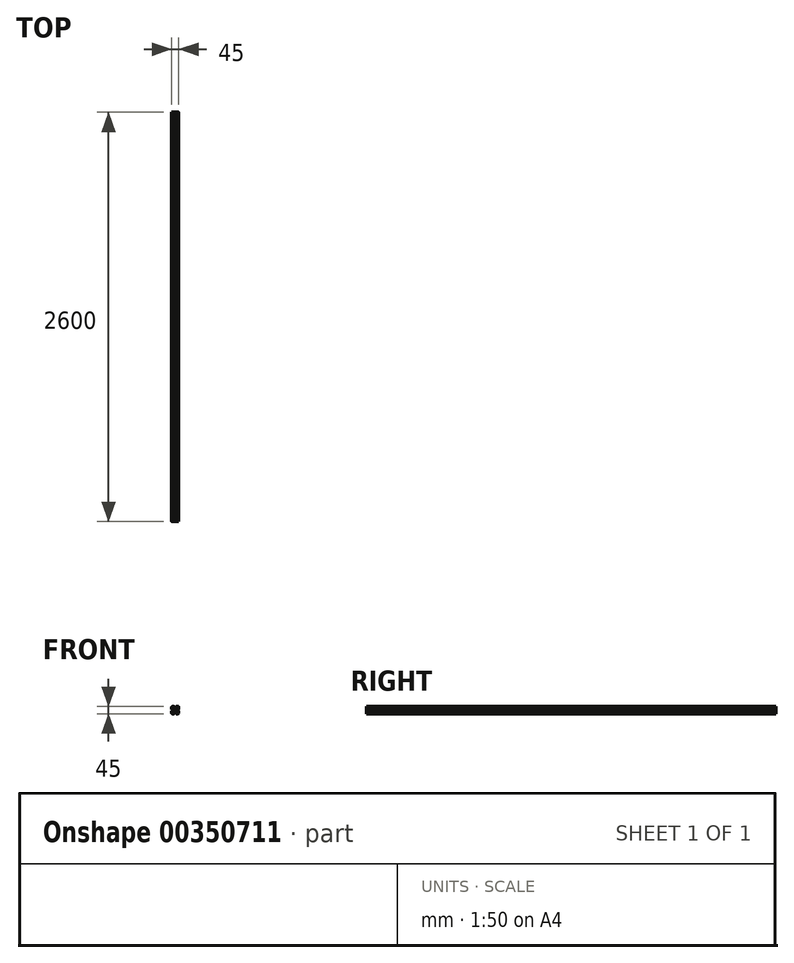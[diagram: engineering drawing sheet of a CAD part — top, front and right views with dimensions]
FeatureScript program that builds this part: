
annotation { "Feature Type Name" : "Feature", "Feature Type Description" : "" }
export const myFeature = defineFeature(function(context is Context, id is Id, definition is map)
    precondition{}
    {
        {
            var Q0;
            Q0=qCreatedBy(makeId("Front.planeOp"),FACE);
            var sketch = newSketch(context, id + "F0", { "sketchPlane" : qUnion([Q0])});
            skLineSegment(sketch, "E0", {"start": v(80.5, 122.5) * mm, "end": v(93.5, 122.5) * mm});
            skLineSegment(sketch, "E1", {"start": v(95, 121) * mm, "end": v(95, 116.5) * mm});
            skLineSegment(sketch, "E2", {"start": v(95, 116.5) * mm, "end": v(90, 116.5) * mm});
            skLineSegment(sketch, "E3", {"start": v(90, 116.5) * mm, "end": v(90, 112.5) * mm});
            skLineSegment(sketch, "E4", {"start": v(90, 112.5) * mm, "end": v(95, 107.5) * mm});
            skLineSegment(sketch, "E5", {"start": v(95, 107.5) * mm, "end": v(100, 107.5) * mm});
            skLineSegment(sketch, "E6", {"start": v(95, 121) * mm, "end": v(94.5, 121) * mm});
            skLineSegment(sketch, "E7", {"start": v(94.5, 121) * mm, "end": v(94.5, 121.5) * mm});
            skPoint(sketch, "E8.orphan", {"position": v(95, 122.5) * mm});
            skPoint(sketch, "E9.visualSharp", {"position": v(94.5, 122.5) * mm});
            skArc(sketch, "E9.filletArc", {"start": v(94.5, 121.5) * mm, "mid": v(94.2, 122.2) * mm, "end": v(93.5, 122.5) * mm});
            skPoint(sketch, "E10.visualSharp", {"position": v(77.5, 122.5) * mm});
            skArc(sketch, "E10.filletArc", {"start": v(80.5, 122.5) * mm, "mid": v(79.35, 122.27) * mm, "end": v(78.38, 121.62) * mm});
            skLineSegment(sketch, "E11.4", {"start": v(-7, 19.5) * mm, "end": v(-7, 19.5) * mm});
            skLineSegment(sketch, "E11.11", {"start": v(-19.5, 7) * mm, "end": v(-19.5, 7) * mm});
            skLineSegment(sketch, "E12", {"start": v(77.5, 122.5) * mm, "end": v(100, 100) * mm, "construction": true});
            skLineSegment(sketch, "E13.MirrorCS", {"start": v(92.5, 105) * mm, "end": v(92.5, 100) * mm});
            skLineSegment(sketch, "E14.MirrorCS", {"start": v(87.5, 110) * mm, "end": v(92.5, 105) * mm});
            skLineSegment(sketch, "E15.MirrorCS", {"start": v(83.5, 110) * mm, "end": v(87.5, 110) * mm});
            skLineSegment(sketch, "E16.MirrorCS", {"start": v(83.5, 105) * mm, "end": v(83.5, 110) * mm});
            skLineSegment(sketch, "E17.MirrorCS", {"start": v(79, 105) * mm, "end": v(83.5, 105) * mm});
            skLineSegment(sketch, "E18.MirrorCS", {"start": v(79, 105) * mm, "end": v(79, 105.5) * mm});
            skLineSegment(sketch, "E19.MirrorCS", {"start": v(79, 105.5) * mm, "end": v(78.5, 105.5) * mm});
            skArc(sketch, "E20.MirrorCS", {"start": v(78.5, 105.5) * mm, "mid": v(77.8, 105.8) * mm, "end": v(77.5, 106.5) * mm});
            skLineSegment(sketch, "E21.MirrorCS", {"start": v(77.5, 119.5) * mm, "end": v(77.5, 106.5) * mm});
            skArc(sketch, "E22.MirrorCS", {"start": v(77.5, 119.5) * mm, "mid": v(77.73, 120.65) * mm, "end": v(78.38, 121.62) * mm});
            skLineSegment(sketch, "E23.MirrorCS", {"start": v(105, 121) * mm, "end": v(105.5, 121) * mm});
            skLineSegment(sketch, "E24.MirrorCS", {"start": v(105.5, 121) * mm, "end": v(105.5, 121.5) * mm});
            skLineSegment(sketch, "E25.MirrorCS", {"start": v(121, 105.5) * mm, "end": v(121.5, 105.5) * mm});
            skLineSegment(sketch, "E26.MirrorCS", {"start": v(121, 105) * mm, "end": v(121, 105.5) * mm});
            skArc(sketch, "E27.MirrorCS", {"start": v(105.5, 121.5) * mm, "mid": v(105.8, 122.2) * mm, "end": v(106.5, 122.5) * mm});
            skLineSegment(sketch, "E28.MirrorCS", {"start": v(110, 116.5) * mm, "end": v(110, 112.5) * mm});
            skArc(sketch, "E29.MirrorCS", {"start": v(122.5, 119.5) * mm, "mid": v(122.27, 120.65) * mm, "end": v(121.62, 121.62) * mm});
            skLineSegment(sketch, "E30.MirrorCS", {"start": v(112.5, 110) * mm, "end": v(107.5, 105) * mm});
            skLineSegment(sketch, "E31.MirrorCS", {"start": v(110, 112.5) * mm, "end": v(105, 107.5) * mm});
            skPoint(sketch, "E32.MirrorP", {"position": v(105.5, 122.5) * mm});
            skLineSegment(sketch, "E33.MirrorCS", {"start": v(105, 116.5) * mm, "end": v(110, 116.5) * mm});
            skArc(sketch, "E34.MirrorCS", {"start": v(119.5, 122.5) * mm, "mid": v(120.65, 122.27) * mm, "end": v(121.62, 121.62) * mm});
            skLineSegment(sketch, "E35.MirrorCS", {"start": v(121, 105) * mm, "end": v(116.5, 105) * mm});
            skLineSegment(sketch, "E36.MirrorCS", {"start": v(122.5, 119.5) * mm, "end": v(122.5, 106.5) * mm});
            skArc(sketch, "E37.MirrorCS", {"start": v(121.5, 105.5) * mm, "mid": v(122.2, 105.8) * mm, "end": v(122.5, 106.5) * mm});
            skLineSegment(sketch, "E38.MirrorCS", {"start": v(107.5, 105) * mm, "end": v(107.5, 100) * mm});
            skLineSegment(sketch, "E39.MirrorCS", {"start": v(116.5, 110) * mm, "end": v(112.5, 110) * mm});
            skPoint(sketch, "E40.MirrorP", {"position": v(122.5, 122.5) * mm});
            skLineSegment(sketch, "E41.MirrorCS", {"start": v(122.5, 122.5) * mm, "end": v(100, 100) * mm, "construction": true});
            skLineSegment(sketch, "E42.MirrorCS", {"start": v(105, 121) * mm, "end": v(105, 116.5) * mm});
            skLineSegment(sketch, "E43.MirrorCS", {"start": v(116.5, 105) * mm, "end": v(116.5, 110) * mm});
            skLineSegment(sketch, "E44.MirrorCS", {"start": v(105, 107.5) * mm, "end": v(100, 107.5) * mm});
            skPoint(sketch, "E45.MirrorP", {"position": v(105, 122.5) * mm});
            skLineSegment(sketch, "E46.MirrorCS", {"start": v(119.5, 122.5) * mm, "end": v(106.5, 122.5) * mm});
            skLineSegment(sketch, "E47.MirrorCS", {"start": v(94.5, 79) * mm, "end": v(94.5, 78.5) * mm});
            skLineSegment(sketch, "E48.MirrorCS", {"start": v(79, 95) * mm, "end": v(79, 94.5) * mm});
            skLineSegment(sketch, "E49.MirrorCS", {"start": v(95, 92.5) * mm, "end": v(100, 92.5) * mm});
            skLineSegment(sketch, "E50.MirrorCS", {"start": v(79, 94.5) * mm, "end": v(78.5, 94.5) * mm});
            skLineSegment(sketch, "E51.MirrorCS", {"start": v(95, 79) * mm, "end": v(94.5, 79) * mm});
            skArc(sketch, "E52.MirrorCS", {"start": v(94.5, 78.5) * mm, "mid": v(94.2, 77.8) * mm, "end": v(93.5, 77.5) * mm});
            skLineSegment(sketch, "E53.MirrorCS", {"start": v(77.5, 80.5) * mm, "end": v(77.5, 93.5) * mm});
            skLineSegment(sketch, "E54.MirrorCS", {"start": v(83.5, 90) * mm, "end": v(87.5, 90) * mm});
            skPoint(sketch, "E55.MirrorP", {"position": v(95, 77.5) * mm});
            skLineSegment(sketch, "E56.MirrorCS", {"start": v(90, 83.5) * mm, "end": v(90, 87.5) * mm});
            skArc(sketch, "E57.MirrorCS", {"start": v(78.5, 94.5) * mm, "mid": v(77.8, 94.2) * mm, "end": v(77.5, 93.5) * mm});
            skLineSegment(sketch, "E58.MirrorCS", {"start": v(80.5, 77.5) * mm, "end": v(93.5, 77.5) * mm});
            skPoint(sketch, "E59.MirrorP", {"position": v(77.5, 77.5) * mm});
            skPoint(sketch, "E60.MirrorP", {"position": v(94.5, 77.5) * mm});
            skLineSegment(sketch, "E61.MirrorCS", {"start": v(87.5, 90) * mm, "end": v(92.5, 95) * mm});
            skLineSegment(sketch, "E62.MirrorCS", {"start": v(90, 87.5) * mm, "end": v(95, 92.5) * mm});
            skLineSegment(sketch, "E63.MirrorCS", {"start": v(95, 79) * mm, "end": v(95, 83.5) * mm});
            skLineSegment(sketch, "E64.MirrorCS", {"start": v(77.5, 77.5) * mm, "end": v(100, 100) * mm, "construction": true});
            skArc(sketch, "E65.MirrorCS", {"start": v(80.5, 77.5) * mm, "mid": v(79.35, 77.73) * mm, "end": v(78.38, 78.38) * mm});
            skArc(sketch, "E66.MirrorCS", {"start": v(77.5, 80.5) * mm, "mid": v(77.73, 79.35) * mm, "end": v(78.38, 78.38) * mm});
            skLineSegment(sketch, "E67.MirrorCS", {"start": v(83.5, 95) * mm, "end": v(83.5, 90) * mm});
            skLineSegment(sketch, "E68.MirrorCS", {"start": v(95, 83.5) * mm, "end": v(90, 83.5) * mm});
            skLineSegment(sketch, "E69.MirrorCS", {"start": v(79, 95) * mm, "end": v(83.5, 95) * mm});
            skLineSegment(sketch, "E70.MirrorCS", {"start": v(121, 95) * mm, "end": v(121, 94.5) * mm});
            skLineSegment(sketch, "E71.MirrorCS", {"start": v(105, 79) * mm, "end": v(105.5, 79) * mm});
            skLineSegment(sketch, "E72.MirrorCS", {"start": v(105.5, 79) * mm, "end": v(105.5, 78.5) * mm});
            skLineSegment(sketch, "E73.MirrorCS", {"start": v(121, 94.5) * mm, "end": v(121.5, 94.5) * mm});
            skArc(sketch, "E74.MirrorCS", {"start": v(105.5, 78.5) * mm, "mid": v(105.8, 77.8) * mm, "end": v(106.5, 77.5) * mm});
            skArc(sketch, "E75.MirrorCS", {"start": v(122.5, 80.5) * mm, "mid": v(122.27, 79.35) * mm, "end": v(121.62, 78.38) * mm});
            skLineSegment(sketch, "E76.MirrorCS", {"start": v(121, 95) * mm, "end": v(116.5, 95) * mm});
            skArc(sketch, "E77.MirrorCS", {"start": v(121.5, 94.5) * mm, "mid": v(122.2, 94.2) * mm, "end": v(122.5, 93.5) * mm});
            skLineSegment(sketch, "E78.MirrorCS", {"start": v(116.5, 90) * mm, "end": v(112.5, 90) * mm});
            skPoint(sketch, "E79.MirrorP", {"position": v(105, 77.5) * mm});
            skPoint(sketch, "E80.MirrorP", {"position": v(105.5, 77.5) * mm});
            skLineSegment(sketch, "E81.MirrorCS", {"start": v(105, 83.5) * mm, "end": v(110, 83.5) * mm});
            skPoint(sketch, "E82.MirrorP", {"position": v(122.5, 77.5) * mm});
            skLineSegment(sketch, "E83.MirrorCS", {"start": v(112.5, 90) * mm, "end": v(107.5, 95) * mm});
            skLineSegment(sketch, "E84.MirrorCS", {"start": v(110, 83.5) * mm, "end": v(110, 87.5) * mm});
            skLineSegment(sketch, "E85.MirrorCS", {"start": v(110, 87.5) * mm, "end": v(105, 92.5) * mm});
            skLineSegment(sketch, "E86.MirrorCS", {"start": v(116.5, 95) * mm, "end": v(116.5, 90) * mm});
            skArc(sketch, "E87.MirrorCS", {"start": v(119.5, 77.5) * mm, "mid": v(120.65, 77.73) * mm, "end": v(121.62, 78.38) * mm});
            skLineSegment(sketch, "E88.MirrorCS", {"start": v(119.5, 77.5) * mm, "end": v(106.5, 77.5) * mm});
            skLineSegment(sketch, "E89.MirrorCS", {"start": v(105, 79) * mm, "end": v(105, 83.5) * mm});
            skLineSegment(sketch, "E90.MirrorCS", {"start": v(122.5, 80.5) * mm, "end": v(122.5, 93.5) * mm});
            skLineSegment(sketch, "E91.MirrorCS", {"start": v(107.5, 95) * mm, "end": v(107.5, 100) * mm});
            skLineSegment(sketch, "E92.MirrorCS", {"start": v(105, 92.5) * mm, "end": v(100, 92.5) * mm});
            skLineSegment(sketch, "E93.MirrorCS", {"start": v(92.5, 95) * mm, "end": v(92.5, 100) * mm});
            skSolve(sketch);
        }
        {
            var Q0;
            Q0=qSketchRegion(id+"F0",true);
            extrude(context, id + "F1", {"entities" : qUnion([Q0]), "depth" : 2600 * mm});
        }
    });
